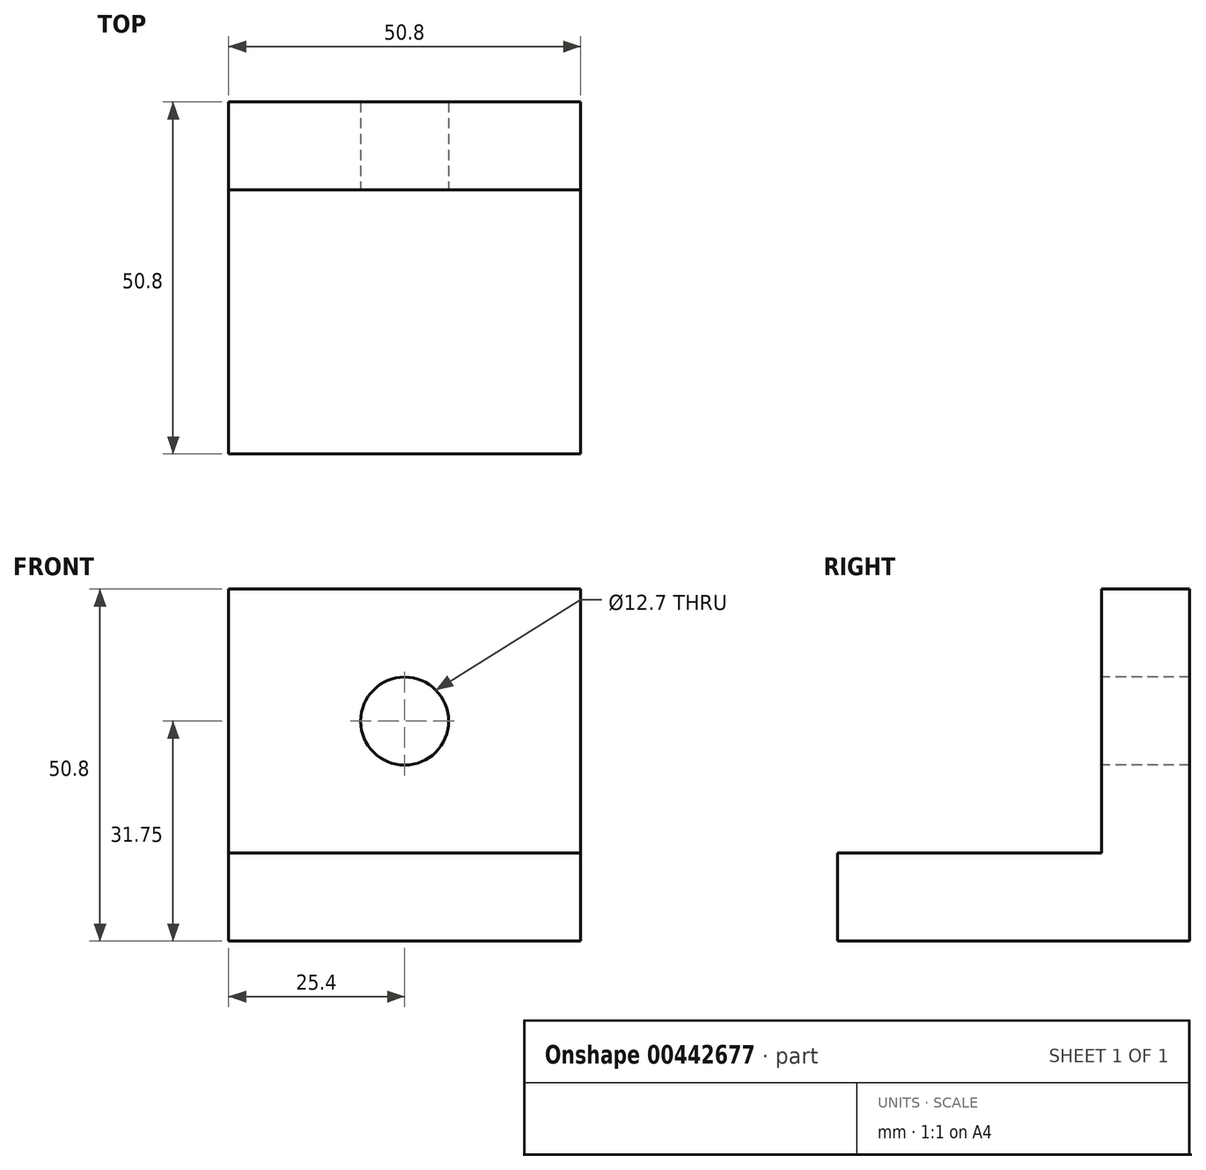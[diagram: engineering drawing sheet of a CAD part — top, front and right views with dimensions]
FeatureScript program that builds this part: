
annotation { "Feature Type Name" : "Feature", "Feature Type Description" : "" }
export const myFeature = defineFeature(function(context is Context, id is Id, definition is map)
    precondition{}
    {
        {
            var Q0;
            Q0=qCreatedBy(makeId("Top.planeOp"),FACE);
            var sketch = newSketch(context, id + "F0", { "sketchPlane" : qUnion([Q0])});
            skLineSegment(sketch, "E0", {"start": v(0, 0) * mm, "end": v(0, -50.8) * mm});
            skLineSegment(sketch, "E1", {"start": v(0, -50.8) * mm, "end": v(50.8, -50.8) * mm});
            skLineSegment(sketch, "E2", {"start": v(50.8, 0) * mm, "end": v(50.8, -50.8) * mm});
            skLineSegment(sketch, "E3", {"start": v(50.8, 0) * mm, "end": v(0, 0) * mm});
            skSolve(sketch);
        }
        {
            var Q0;
            Q0 = qSketchRegion(id + "F0", true);
            extrude(context, id + "F1", {"entities" : qUnion([Q0]), "depth" : 12.7 * mm});
        }
        {
            var Q0;
            Q0=makeQuery(id+"F1.opExtrude","CAP_FACE",FACE,{"disambiguationData":[OSD([sQuery(id+"F0.wireOp",EDGE,"E0"),sQuery(id+"F0.wireOp",EDGE,"E1"),sQuery(id+"F0.wireOp",EDGE,"E2"),sQuery(id+"F0.wireOp",EDGE,"E3")])],"isStart":false});
            var sketch = newSketch(context, id + "F2", { "sketchPlane" : qUnion([Q0])});
            skLineSegment(sketch, "E4", {"start": v(0, 0) * mm, "end": v(0, -12.7) * mm});
            skLineSegment(sketch, "E5", {"start": v(0, -12.7) * mm, "end": v(50.8, -12.7) * mm});
            skLineSegment(sketch, "E6", {"start": v(50.8, -12.7) * mm, "end": v(50.8, 0) * mm});
            skLineSegment(sketch, "E7", {"start": v(50.8, 0) * mm, "end": v(0, 0) * mm});
            skSolve(sketch);
        }
        {
            var Q0;
            Q0 = qSketchRegion(id + "F2", true);
            extrude(context, id + "F3", {"entities" : qUnion([Q0]), "operationType" : NewBodyOperationType.ADD, "depth" : 38.1 * mm});
        }
        {
            var Q0;
            Q0=makeQuery(id+"F3.opExtrude","SWEPT_FACE",FACE,{"disambiguationData":[OSD([sQuery(id+"F2.wireOp",EDGE,"E5")])]});
            var sketch = newSketch(context, id + "F4", { "sketchPlane" : qUnion([Q0])});
            skLineSegment(sketch, "E8", {"start": v(25.4, 50.8) * mm, "end": v(25.4, 31.75) * mm});
            skPoint(sketch, "E8.endSnap0", {"position": v(0, 31.75) * mm});
            skCircle(sketch, "E9", {"center": v(25.4, 31.75) * mm, "radius": 6.35 * mm});
            skSolve(sketch);
        }
        {
            var Q0;
            Q0 = qSketchRegion(id + "F4", true);
            extrude(context, id + "F5", {"entities" : qUnion([Q0]), "operationType" : NewBodyOperationType.REMOVE, "oppositeDirection" : true, "depth" : 55.88 * mm});
        }
    });
